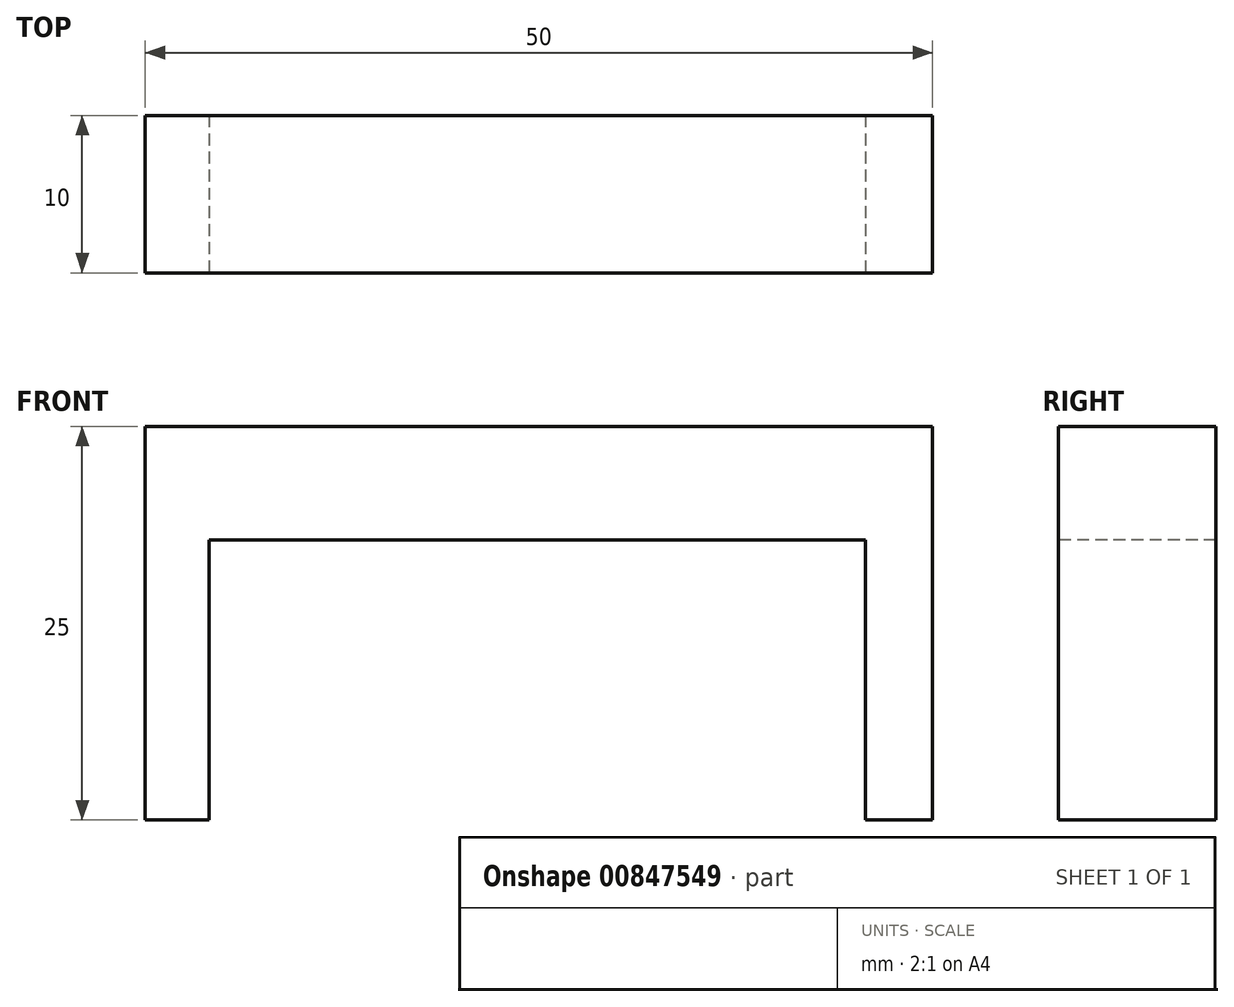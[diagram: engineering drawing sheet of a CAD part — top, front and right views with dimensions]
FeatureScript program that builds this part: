
annotation { "Feature Type Name" : "Feature", "Feature Type Description" : "" }
export const myFeature = defineFeature(function(context is Context, id is Id, definition is map)
    precondition{}
    {
        {
            var Q0;
            Q0=qCreatedBy(makeId("Top.planeOp"),FACE);
            var sketch = newSketch(context, id + "F0", { "sketchPlane" : qUnion([Q0])});
            skLineSegment(sketch, "E0.bottom", {"start": v(-25, -5) * mm, "end": v(25, -5) * mm});
            skLineSegment(sketch, "E0.top", {"start": v(-25, 5) * mm, "end": v(25, 5) * mm});
            skLineSegment(sketch, "E0.left", {"start": v(-25, -5) * mm, "end": v(-25, 5) * mm});
            skLineSegment(sketch, "E0.right", {"start": v(25, -5) * mm, "end": v(25, 5) * mm});
            skPoint(sketch, "E0.middle", {"position": v(0, 0) * mm});
            skSolve(sketch);
        }
        {
            var Q0;
            Q0=makeQuery(id+"F0.imprint","IMPRINT",FACE,{"disambiguationData":[TD([[makeQuery(id+"F0.imprint","IMPRINT",EDGE,{"derivedFrom":sQuery(id+"F0.wireOp",EDGE,"E0.bottom")}),1.0]])]});
            extrude(context, id + "F1", {"entities" : qUnion([Q0]), "depth" : 25 * mm, "offsetDistance" : 25 * mm});
        }
        {
            var Q0;
            Q0=makeQuery(id+"F1.opExtrude","SWEPT_FACE",FACE,{"disambiguationData":[OSD([sQuery(id+"F0.wireOp",EDGE,"E0.bottom")])]});
            var sketch = newSketch(context, id + "F2", { "sketchPlane" : qUnion([Q0])});
            skLineSegment(sketch, "E1.bottom", {"start": v(-20.95, 17.8) * mm, "end": v(20.74, 17.8) * mm});
            skLineSegment(sketch, "E1.top", {"start": v(-20.95, 0) * mm, "end": v(20.74, 0) * mm});
            skLineSegment(sketch, "E1.left", {"start": v(-20.95, 17.8) * mm, "end": v(-20.95, 0) * mm});
            skLineSegment(sketch, "E1.right", {"start": v(20.74, 17.8) * mm, "end": v(20.74, 0) * mm});
            skSolve(sketch);
        }
        {
            var Q0;
            Q0=makeQuery(id+"F2.imprint","IMPRINT",FACE,{"disambiguationData":[TD([[makeQuery(id+"F2.imprint","IMPRINT",EDGE,{"derivedFrom":sQuery(id+"F2.wireOp",EDGE,"E1.bottom")}),-1.0]])]});
            extrude(context, id + "F3", {"entities" : qUnion([Q0]), "operationType" : NewBodyOperationType.REMOVE, "endBound" : BoundingType.THROUGH_ALL, "oppositeDirection" : true, "depth" : 25 * mm, "offsetDistance" : 25 * mm});
        }
    });
